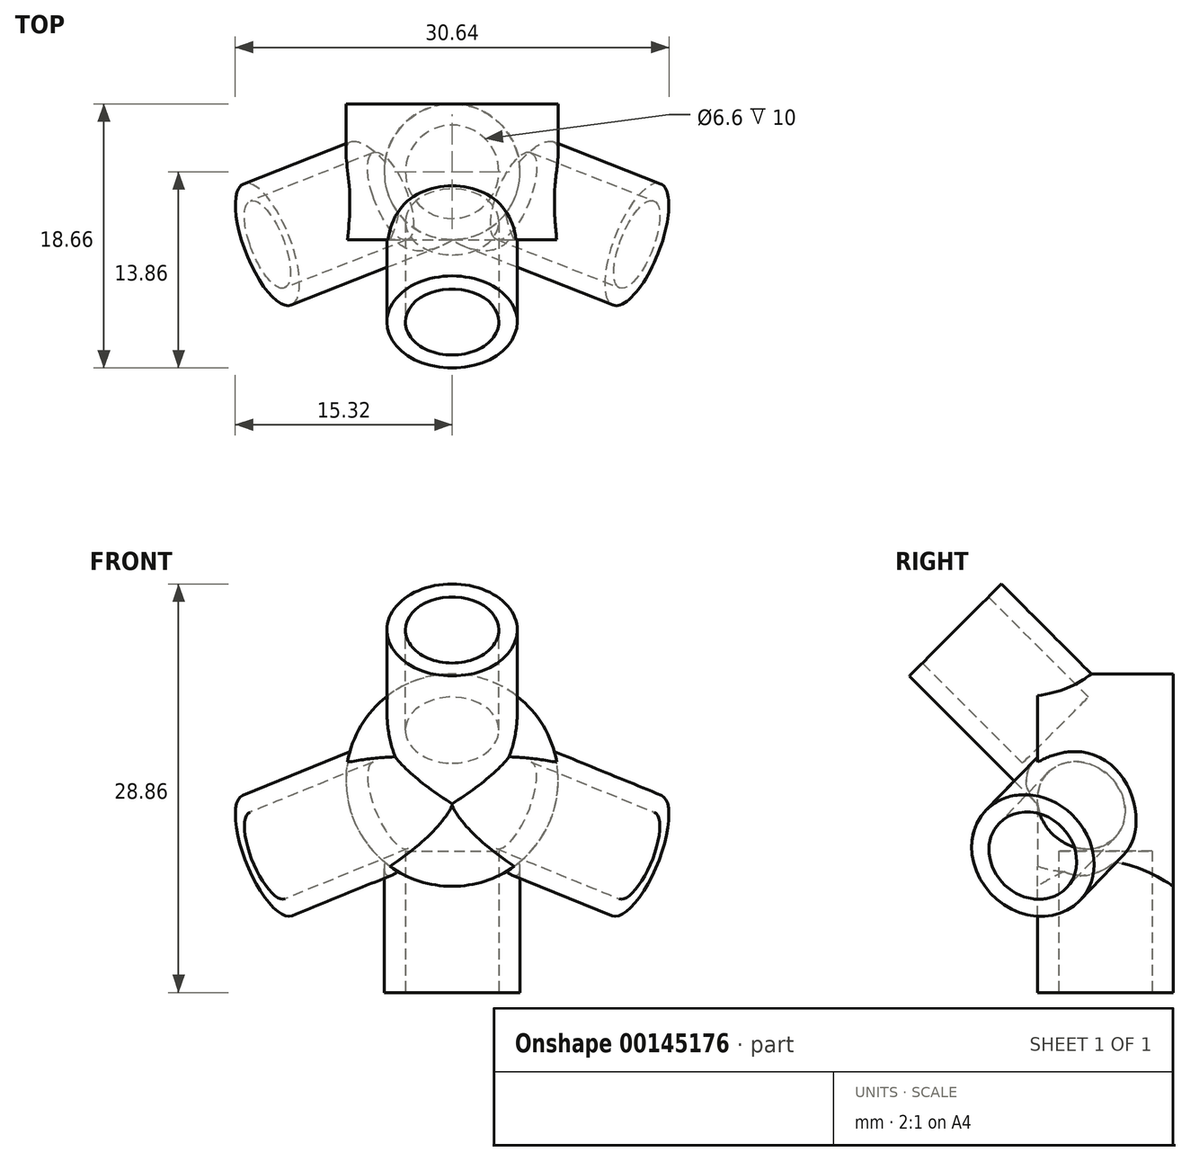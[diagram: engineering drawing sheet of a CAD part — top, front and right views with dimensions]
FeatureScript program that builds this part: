
annotation { "Feature Type Name" : "Feature", "Feature Type Description" : "" }
export const myFeature = defineFeature(function(context is Context, id is Id, definition is map)
    precondition{}
    {
        {
            var Q0;
            Q0=qCreatedBy(makeId("Front.planeOp"),FACE);
            var sketch = newSketch(context, id + "F0", { "sketchPlane" : qUnion([Q0])});
            skLineSegment(sketch, "E0", {"start": v(0, 0) * mm, "end": v(0, -50) * mm, "construction": true});
            skLineSegment(sketch, "E1.bottom", {"start": v(0, 0) * mm, "end": v(-4.8, 0) * mm});
            skLineSegment(sketch, "E1.top", {"start": v(0, -15) * mm, "end": v(-4.8, -15) * mm});
            skLineSegment(sketch, "E1.left", {"start": v(0, 0) * mm, "end": v(0, -15) * mm});
            skLineSegment(sketch, "E1.right", {"start": v(-4.8, 0) * mm, "end": v(-4.8, -15) * mm});
            skSolve(sketch);
        }
        {
            var Q0;
            Q0=qCreatedBy(makeId("Front.planeOp"),FACE);
            var Q1;
            Q1=qCreatedBy(makeId("Top.planeOp"),FACE);
            cPlane(context, id + "F1", {"entities" : qUnion([Q0, Q1]), "cplaneType" : CPlaneType.MID_PLANE, "offset" : 25 * mm, "width" : 150 * mm, "height" : 150 * mm});
        }
        {
            var Q0;
            Q0=qCreatedBy(id+"F1.planeOp",FACE);
            var sketch = newSketch(context, id + "F2", { "sketchPlane" : qUnion([Q0])});
            skLineSegment(sketch, "E2", {"start": v(0, 0) * mm, "end": v(0, 50) * mm, "construction": true});
            skLineSegment(sketch, "E3.bottom", {"start": v(0, 0) * mm, "end": v(-4.6, 0) * mm});
            skLineSegment(sketch, "E3.top", {"start": v(0, 15) * mm, "end": v(-4.6, 15) * mm});
            skLineSegment(sketch, "E3.left", {"start": v(0, 0) * mm, "end": v(0, 15) * mm});
            skLineSegment(sketch, "E3.right", {"start": v(-4.6, 0) * mm, "end": v(-4.6, 15) * mm});
            skSolve(sketch);
        }
        {
            var Q0;
            Q0 = qSketchRegion(id + "F2", true);
            var Q1;
            Q1=sQuery(id+"F2.wireOp",EDGE,"E2");
            revolve(context, id + "F3", {"entities" : qUnion([Q0]), "axis" : qUnion([Q1]), "revolveType" : RevolveType.FULL});
        }
        {
            var Q0;
            Q0 = qSketchRegion(id + "F0", true);
            var Q1;
            Q1=sQuery(id+"F0.wireOp",EDGE,"E0");
            revolve(context, id + "F4", {"operationType" : NewBodyOperationType.ADD, "entities" : qUnion([Q0]), "axis" : qUnion([Q1]), "revolveType" : RevolveType.FULL});
        }
        {
            var Q0;
            Q0=qCreatedBy(makeId("Top.planeOp"),FACE);
            var sketch = newSketch(context, id + "F5", { "sketchPlane" : qUnion([Q0])});
            skLineSegment(sketch, "E4", {"start": v(0, 0) * mm, "end": v(0, -50) * mm, "construction": true});
            skSolve(sketch);
        }
        {
            var Q0;
            Q0=qCreatedBy(makeId("Front.planeOp"),FACE);
            var sketch = newSketch(context, id + "F6", { "sketchPlane" : qUnion([Q0])});
            skLineSegment(sketch, "E5", {"start": v(0, 0) * mm, "end": v(46.3, -18.9) * mm, "construction": true});
            skLineSegment(sketch, "E6", {"start": v(0, 0) * mm, "end": v(-46.3, -18.9) * mm, "construction": true});
            skSolve(sketch);
        }
        {
            var Q0;
            Q0=sQuery(id+"F6.wireOp",VERTEX,"E5.end");
            var Q1;
            Q1=sQuery(id+"F6.wireOp",VERTEX,"E5.start");
            var Q2;
            Q2=sQuery(id+"F5.wireOp",VERTEX,"E4.end");
            cPlane(context, id + "F7", {"entities" : qUnion([Q0, Q1, Q2]), "cplaneType" : CPlaneType.THREE_POINT, "offset" : 25 * mm, "width" : 150 * mm, "height" : 150 * mm});
        }
        {
            var Q0;
            Q0=qCreatedBy(id+"F7.planeOp",FACE);
            var sketch = newSketch(context, id + "F8", { "sketchPlane" : qUnion([Q0])});
            skLineSegment(sketch, "E7", {"start": v(0, 0) * mm, "end": v(46.98, 17.1) * mm, "construction": true});
            skLineSegment(sketch, "E8", {"start": v(0, 0) * mm, "end": v(-1.57, 4.32) * mm});
            skLineSegment(sketch, "E9", {"start": v(-1.57, 4.32) * mm, "end": v(12.52, 9.45) * mm});
            skLineSegment(sketch, "E10", {"start": v(12.52, 9.45) * mm, "end": v(14.1, 5.13) * mm});
            skLineSegment(sketch, "E11", {"start": v(14.1, 5.13) * mm, "end": v(0, 0) * mm});
            skSolve(sketch);
        }
        {
            var Q0;
            Q0 = qSketchRegion(id + "F8", true);
            var Q1;
            Q1=sQuery(id+"F8.wireOp",EDGE,"E7");
            revolve(context, id + "F9", {"operationType" : NewBodyOperationType.ADD, "entities" : qUnion([Q0]), "axis" : qUnion([Q1]), "revolveType" : RevolveType.FULL});
        }
        {
            var Q0;
            Q0=sQuery(id+"F6.wireOp",VERTEX,"E6.end");
            var Q1;
            Q1=sQuery(id+"F6.wireOp",VERTEX,"E5.start");
            var Q2;
            Q2=sQuery(id+"F5.wireOp",VERTEX,"E4.end");
            cPlane(context, id + "F10", {"entities" : qUnion([Q0, Q1, Q2]), "cplaneType" : CPlaneType.THREE_POINT, "offset" : 25 * mm, "width" : 150 * mm, "height" : 150 * mm});
        }
        {
            var Q0;
            Q0=qCreatedBy(id+"F10.planeOp",FACE);
            var sketch = newSketch(context, id + "F11", { "sketchPlane" : qUnion([Q0])});
            skLineSegment(sketch, "E12", {"start": v(0, 0) * mm, "end": v(-46.98, -17.1) * mm, "construction": true});
            skLineSegment(sketch, "E13", {"start": v(0, 0) * mm, "end": v(1.97, -5.42) * mm, "construction": true});
            skLineSegment(sketch, "E14", {"start": v(0, 0) * mm, "end": v(1.57, -4.32) * mm});
            skLineSegment(sketch, "E15", {"start": v(1.57, -4.32) * mm, "end": v(-12.52, -9.45) * mm});
            skLineSegment(sketch, "E16", {"start": v(-12.52, -9.45) * mm, "end": v(-14.1, -5.13) * mm});
            skLineSegment(sketch, "E17", {"start": v(-14.1, -5.13) * mm, "end": v(0, 0) * mm});
            skSolve(sketch);
        }
        {
            var Q0;
            Q0 = qSketchRegion(id + "F11", true);
            var Q1;
            Q1=sQuery(id+"F11.wireOp",EDGE,"E12");
            revolve(context, id + "F12", {"operationType" : NewBodyOperationType.ADD, "entities" : qUnion([Q0]), "axis" : qUnion([Q1]), "revolveType" : RevolveType.FULL});
        }
        {
            var Q0;
            Q0=qCreatedBy(makeId("Front.planeOp"),FACE);
            var sketch = newSketch(context, id + "F13", { "sketchPlane" : qUnion([Q0])});
            skCircle(sketch, "E18", {"center": v(0, 0) * mm, "radius": 7.5 * mm});
            skSolve(sketch);
        }
        {
            var Q0;
            Q0 = qSketchRegion(id + "F13", true);
            extrude(context, id + "F14", {"entities" : qUnion([Q0]), "operationType" : NewBodyOperationType.ADD, "endBound" : BoundingType.SYMMETRIC, "depth" : 9.6 * mm});
        }
        {
            var Q0;
            Q0=makeQuery(id+"F9.opRevolve","SWEPT_FACE",FACE,{"disambiguationData":[OSD([sQuery(id+"F8.wireOp",EDGE,"E10")])]});
            var sketch = newSketch(context, id + "F15", { "sketchPlane" : qUnion([Q0])});
            skCircle(sketch, "E19", {"center": v(0, 0) * mm, "radius": 3.3 * mm});
            skSolve(sketch);
        }
        {
            var Q0;
            Q0=makeQuery(id+"F15.imprint","IMPRINT",FACE,{"disambiguationData":[TD([[makeQuery(id+"F15.imprint","IMPRINT",EDGE,{"derivedFrom":sQuery(id+"F15.wireOp",EDGE,"E19")}),1.0]])]});
            extrude(context, id + "F16", {"entities" : qUnion([Q0]), "operationType" : NewBodyOperationType.REMOVE, "oppositeDirection" : true, "depth" : 10 * mm});
        }
        {
            var Q0;
            Q0=makeQuery(id+"F3.opRevolve","SWEPT_FACE",FACE,{"disambiguationData":[OSD([sQuery(id+"F2.wireOp",EDGE,"E3.top")])]});
            var sketch = newSketch(context, id + "F17", { "sketchPlane" : qUnion([Q0])});
            skCircle(sketch, "E20", {"center": v(0, 0) * mm, "radius": 3.3 * mm});
            skSolve(sketch);
        }
        {
            var Q0;
            Q0 = qSketchRegion(id + "F17", true);
            extrude(context, id + "F18", {"entities" : qUnion([Q0]), "operationType" : NewBodyOperationType.REMOVE, "oppositeDirection" : true, "depth" : 10 * mm});
        }
        {
            var Q0;
            Q0=makeQuery(id+"F12.opRevolve","SWEPT_FACE",FACE,{"disambiguationData":[OSD([sQuery(id+"F11.wireOp",EDGE,"E16")])]});
            var sketch = newSketch(context, id + "F19", { "sketchPlane" : qUnion([Q0])});
            skCircle(sketch, "E21", {"center": v(0, 0) * mm, "radius": 3.3 * mm});
            skSolve(sketch);
        }
        {
            var Q0;
            Q0=makeQuery(id+"F19.imprint","IMPRINT",FACE,{"disambiguationData":[TD([[makeQuery(id+"F19.imprint","IMPRINT",EDGE,{"derivedFrom":sQuery(id+"F19.wireOp",EDGE,"E21")}),1.0]])]});
            extrude(context, id + "F20", {"entities" : qUnion([Q0]), "operationType" : NewBodyOperationType.REMOVE, "oppositeDirection" : true, "depth" : 10 * mm});
        }
        {
            var Q0;
            Q0=makeQuery(id+"F4.opRevolve","SWEPT_FACE",FACE,{"disambiguationData":[OSD([sQuery(id+"F0.wireOp",EDGE,"E1.top")])]});
            var sketch = newSketch(context, id + "F21", { "sketchPlane" : qUnion([Q0])});
            skCircle(sketch, "E22", {"center": v(0, 0) * mm, "radius": 3.3 * mm});
            skSolve(sketch);
        }
        {
            var Q0;
            Q0 = qSketchRegion(id + "F21", true);
            extrude(context, id + "F22", {"entities" : qUnion([Q0]), "operationType" : NewBodyOperationType.REMOVE, "oppositeDirection" : true, "depth" : 10 * mm});
        }
        {
            var Q0;
            Q0=sQuery(id+"F19.wireOp",VERTEX,"E21.center");
            var Q1;
            Q1=sQuery(id+"F6.wireOp",VERTEX,"E6.start");
            var Q2;
            Q2=sQuery(id+"F15.wireOp",VERTEX,"E19.center");
            cPlane(context, id + "F23", {"entities" : qUnion([Q0, Q1, Q2]), "cplaneType" : CPlaneType.THREE_POINT, "offset" : 25 * mm, "width" : 150 * mm, "height" : 150 * mm});
        }
    });
